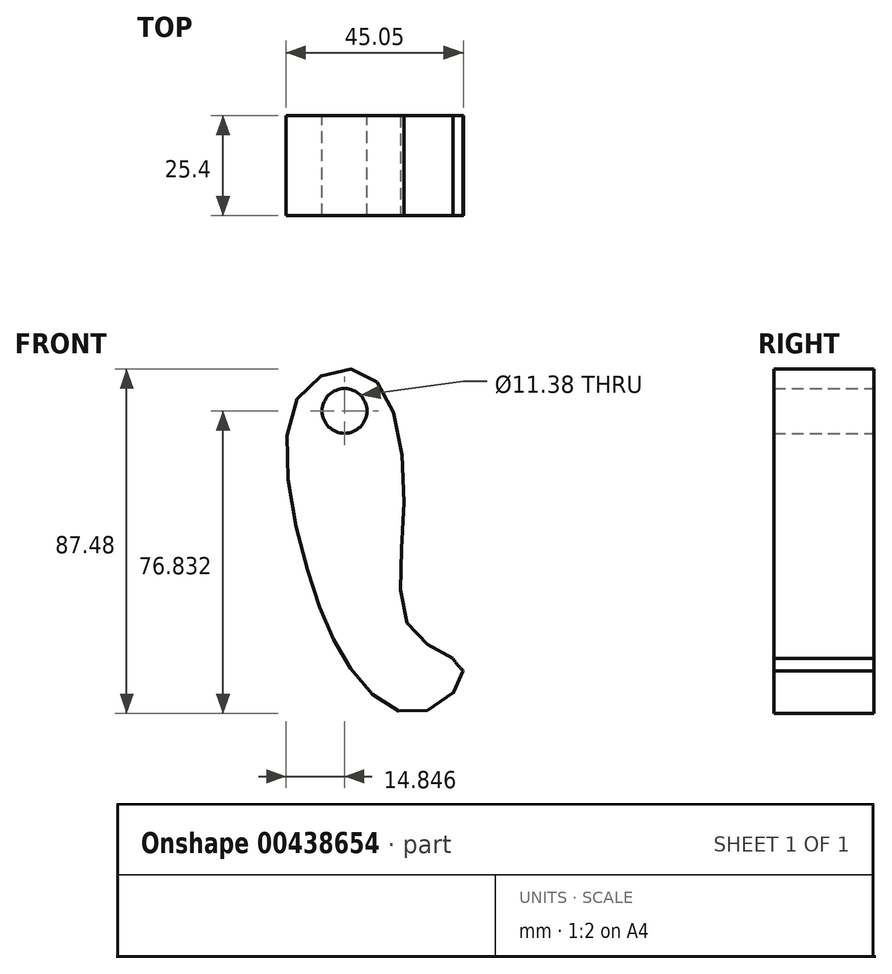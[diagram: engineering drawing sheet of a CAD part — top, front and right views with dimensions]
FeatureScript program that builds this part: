
annotation { "Feature Type Name" : "Feature", "Feature Type Description" : "" }
export const myFeature = defineFeature(function(context is Context, id is Id, definition is map)
    precondition{}
    {
        {
            var Q0;
            Q0=qCreatedBy(makeId("Front.planeOp"),FACE);
            var sketch = newSketch(context, id + "F0", { "sketchPlane" : qUnion([Q0])});
            skCircle(sketch, "E0", {"center": v(0, 0) * mm, "radius": 19 * mm});
            skFitSpline(sketch, "E1", {"points": [v(-13.08, -13.78) * mm, v(-24.86, -24.5) * mm, v(-41.8, -12.97) * mm, v(-53.32, 14.41) * mm, v(-55.12, 55.48) * mm, v(-37.47, 61.6) * mm, v(-28.1, 28.46) * mm, v(-25.58, -4.32) * mm, v(-13.08, -13.78) * mm]});
            skCircle(sketch, "E2", {"center": v(-43.23, 52.24) * mm, "radius": 5.69 * mm});
            skSolve(sketch);
        }
        {
            var Q0;
            Q0=makeQuery(id+"F0.imprint","IMPRINT",FACE,{"disambiguationData":[TD([[makeQuery(id+"F0.imprint","IMPRINT",EDGE,{"derivedFrom":sQuery(id+"F0.wireOp",EDGE,"E2")}),-1.0]])]});
            extrude(context, id + "F1", {"entities" : qUnion([Q0]), "depth" : 25.4 * mm});
        }
    });
